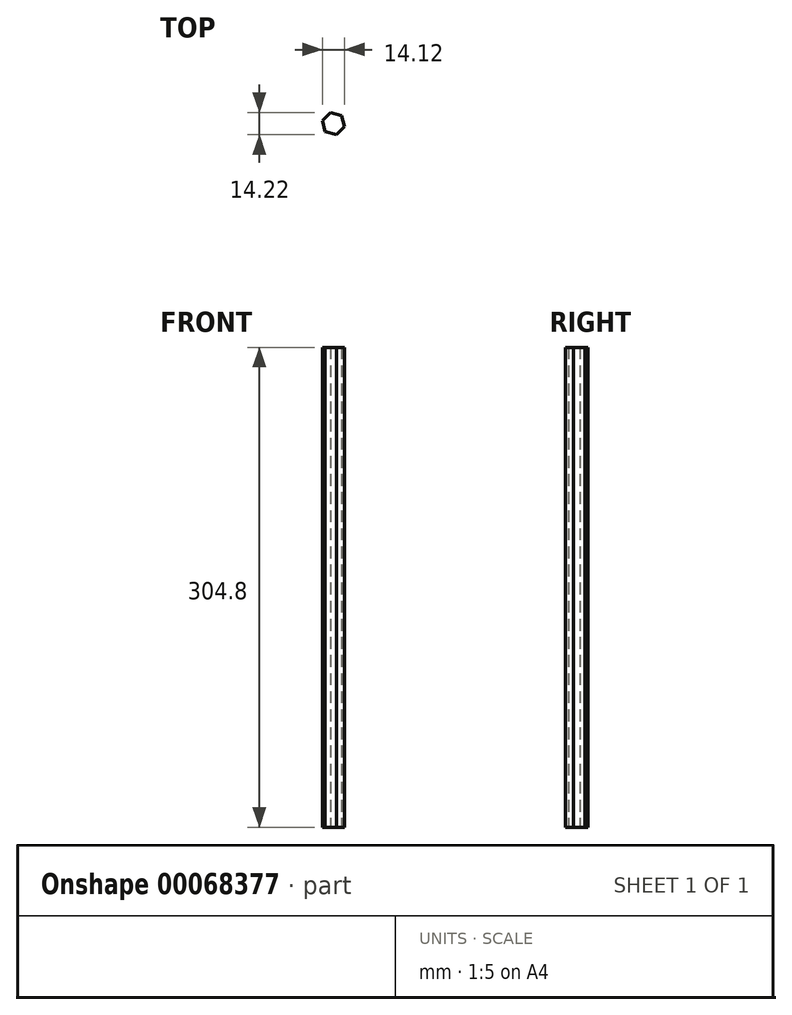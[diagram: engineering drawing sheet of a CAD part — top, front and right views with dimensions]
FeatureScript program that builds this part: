
annotation { "Feature Type Name" : "Feature", "Feature Type Description" : "" }
export const myFeature = defineFeature(function(context is Context, id is Id, definition is map)
    precondition{}
    {
        {
            var Q0;
            Q0=qCreatedBy(makeId("Top.planeOp"),FACE);
            var sketch = newSketch(context, id + "F0", { "sketchPlane" : qUnion([Q0])});
            skCircle(sketch, "E0.cCircle", {"center": v(0, 0) * mm, "radius": 6.35 * mm, "construction": true});
            skLineSegment(sketch, "E0.0", {"start": v(7.06, -2) * mm, "end": v(1.8, -7.1) * mm});
            skLineSegment(sketch, "E0.1", {"start": v(1.8, -7.1) * mm, "end": v(-5.25, -5.12) * mm});
            skLineSegment(sketch, "E0.2", {"start": v(-5.25, -5.12) * mm, "end": v(-7.06, 2) * mm});
            skLineSegment(sketch, "E0.3", {"start": v(-7.06, 2) * mm, "end": v(-1.8, 7.1) * mm});
            skLineSegment(sketch, "E0.4", {"start": v(-1.8, 7.1) * mm, "end": v(5.25, 5.12) * mm});
            skLineSegment(sketch, "E0.5", {"start": v(5.25, 5.12) * mm, "end": v(7.06, -2) * mm});
            skPoint(sketch, "E0.0.midPoint", {"position": v(4.43, -4.55) * mm});
            skSolve(sketch);
        }
        {
            var Q0;
            Q0 = qSketchRegion(id + "F0", true);
            extrude(context, id + "F1", {"entities" : qUnion([Q0]), "depth" : 304.8 * mm});
        }
    });
